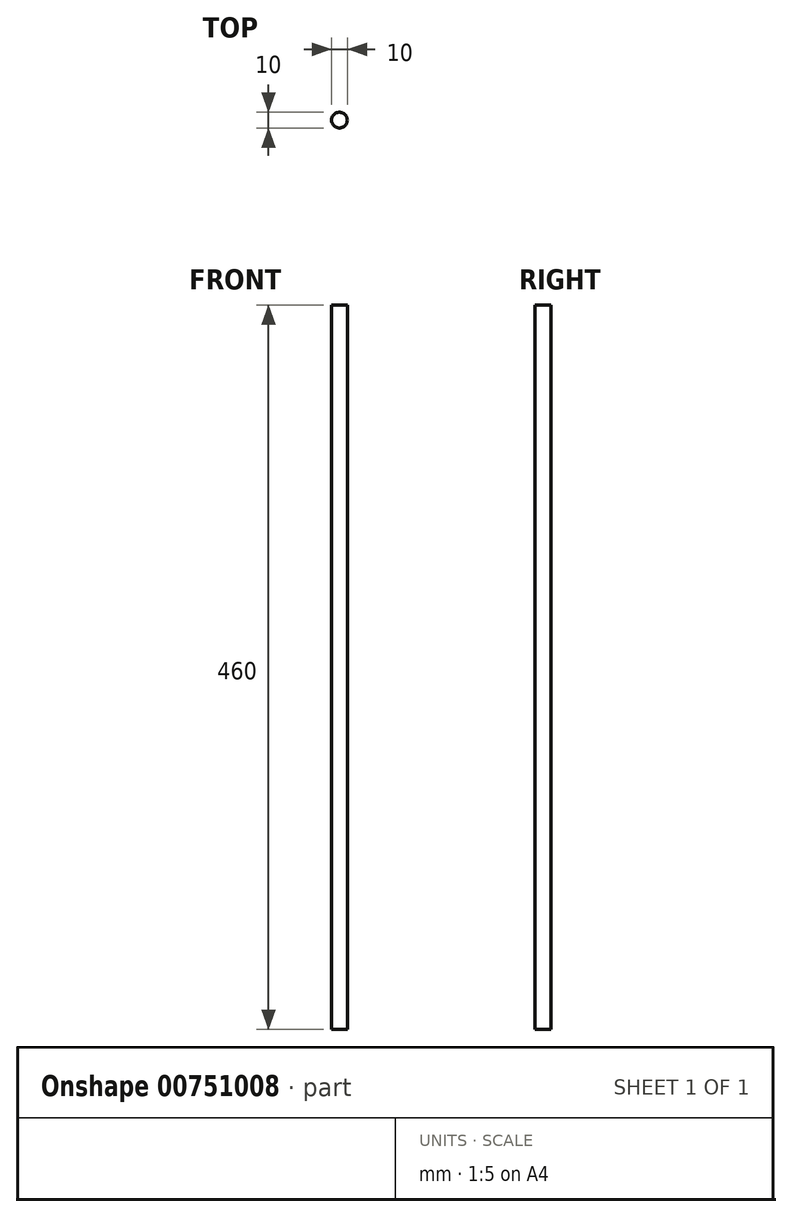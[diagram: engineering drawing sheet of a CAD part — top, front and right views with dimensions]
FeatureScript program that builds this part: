
annotation { "Feature Type Name" : "Feature", "Feature Type Description" : "" }
export const myFeature = defineFeature(function(context is Context, id is Id, definition is map)
    precondition{}
    {
        {
            var Q0;
            Q0=qCreatedBy(makeId("Top.planeOp"),FACE);
            var sketch = newSketch(context, id + "F0", { "sketchPlane" : qUnion([Q0])});
            skCircle(sketch, "E0", {"center": v(0, 0) * mm, "radius": 5 * mm});
            skSolve(sketch);
        }
        {
            var Q0;
            Q0=makeQuery(id+"F0.imprint","IMPRINT",FACE,{"disambiguationData":[TD([[makeQuery(id+"F0.imprint","IMPRINT",EDGE,{"derivedFrom":sQuery(id+"F0.wireOp",EDGE,"E0")}),1.0]])]});
            extrude(context, id + "F1", {"entities" : qUnion([Q0]), "depth" : 460 * mm, "offsetDistance" : 25 * mm});
        }
    });
